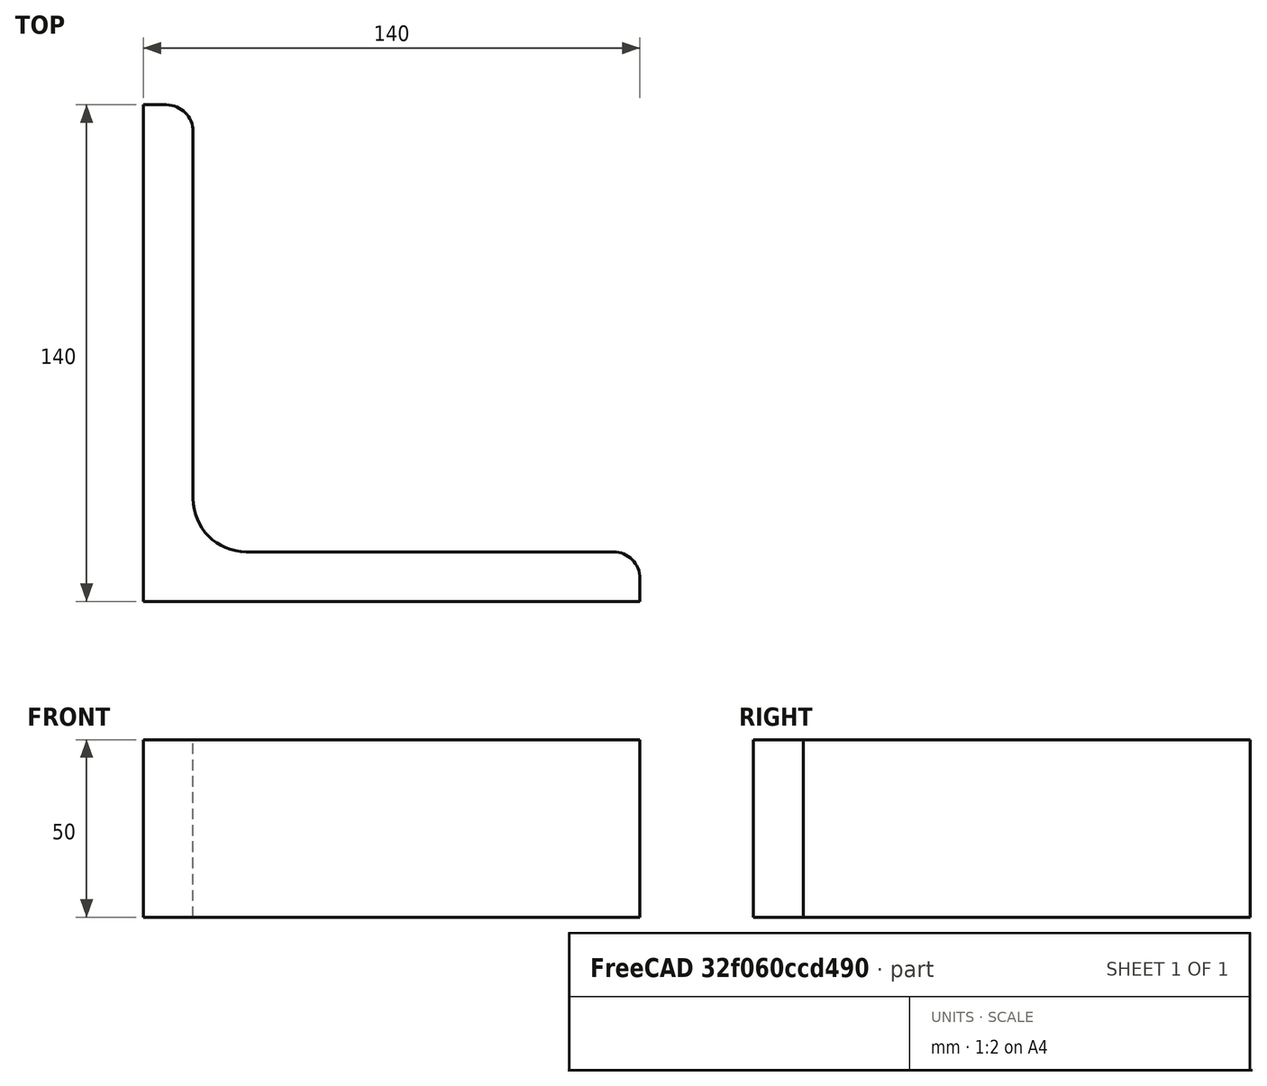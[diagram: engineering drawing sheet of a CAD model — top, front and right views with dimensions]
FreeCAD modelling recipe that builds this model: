
FCSTD DOCUMENT  (FreeCAD 0.15R4671 (Git))
Label: Angle Bar L140x140x14 EN10056 S235JR
License: All rights reserved
LicenseURL: http://en.wikipedia.org/wiki/All_rights_reserved
objects: Sketcher::SketchObject×1, Part::Extrusion×1
note: 2 computed .brp shape members not serialized (recipe doc carries the construction recipe); baked Part::Feature solids carry a one-line shape summary decoded from their .brp

FEATURE [Sketcher::SketchObject] Sketch
  sketch-geometry (9):
    g0: LineSegment StartX=0 StartY=0 StartZ=0 EndX=140 EndY=0 EndZ=0
    g1: LineSegment StartX=140 StartY=0 StartZ=0 EndX=140 EndY=6.5 EndZ=0
    g2: LineSegment StartX=132.5 StartY=14 StartZ=0 EndX=29 EndY=14 EndZ=0
    g3: LineSegment StartX=0 StartY=0 StartZ=0 EndX=0 EndY=140 EndZ=0
    g4: LineSegment StartX=0 StartY=140 StartZ=0 EndX=6.5 EndY=140 EndZ=0
    g5: LineSegment StartX=14 StartY=132.5 StartZ=0 EndX=14 EndY=29 EndZ=0
    g6: ArcOfCircle CenterX=29 CenterY=29 CenterZ=0 NormalX=0 NormalY=0 NormalZ=1 Radius=15 StartAngle=3.14159 EndAngle=4.71239
    g7: ArcOfCircle CenterX=6.5 CenterY=132.5 CenterZ=0 NormalX=0 NormalY=0 NormalZ=1 Radius=7.5 StartAngle=0 EndAngle=1.5708
    g8: ArcOfCircle CenterX=132.5 CenterY=6.5 CenterZ=0 NormalX=0 NormalY=0 NormalZ=1 Radius=7.5 StartAngle=0 EndAngle=1.5708
  constraints (23):
    c: Coincident(g0,g-1)
    c: Horizontal(g0)
    c: Coincident(g1,g0)
    c: Vertical(g1)
    c: Horizontal(g2)
    c: Coincident(g3,g-1)
    c: Vertical(g3)
    c: Coincident(g4,g3)
    c: Horizontal(g4)
    c: Vertical(g5)
    c: Tangent(g5,g6) = -1.5708
    c: Tangent(g2,g6) = 1.5708
    c: Tangent(g4,g7) = 1.5708
    c: Tangent(g5,g7) = 1.5708
    c: Tangent(g2,g8) = -1.5708
    c: Tangent(g1,g8) = -1.5708
    c: DistanceX(g0) = 140
    c: DistanceY(g3) = 140
    c: DistanceY(g0,g2) = 14
    c: DistanceX(g3,g5) = 14
    c: Radius(g6) = 15
    c: Radius(g8) = 7.5
    c: Radius(g7) = 7.5
FEATURE [Part::Extrusion] Extrude  label="Angle Bar L140x140x14 EN10056 S235JR"
  Base = -> Sketch
  Dir = (0,0,50)
  Solid = true
